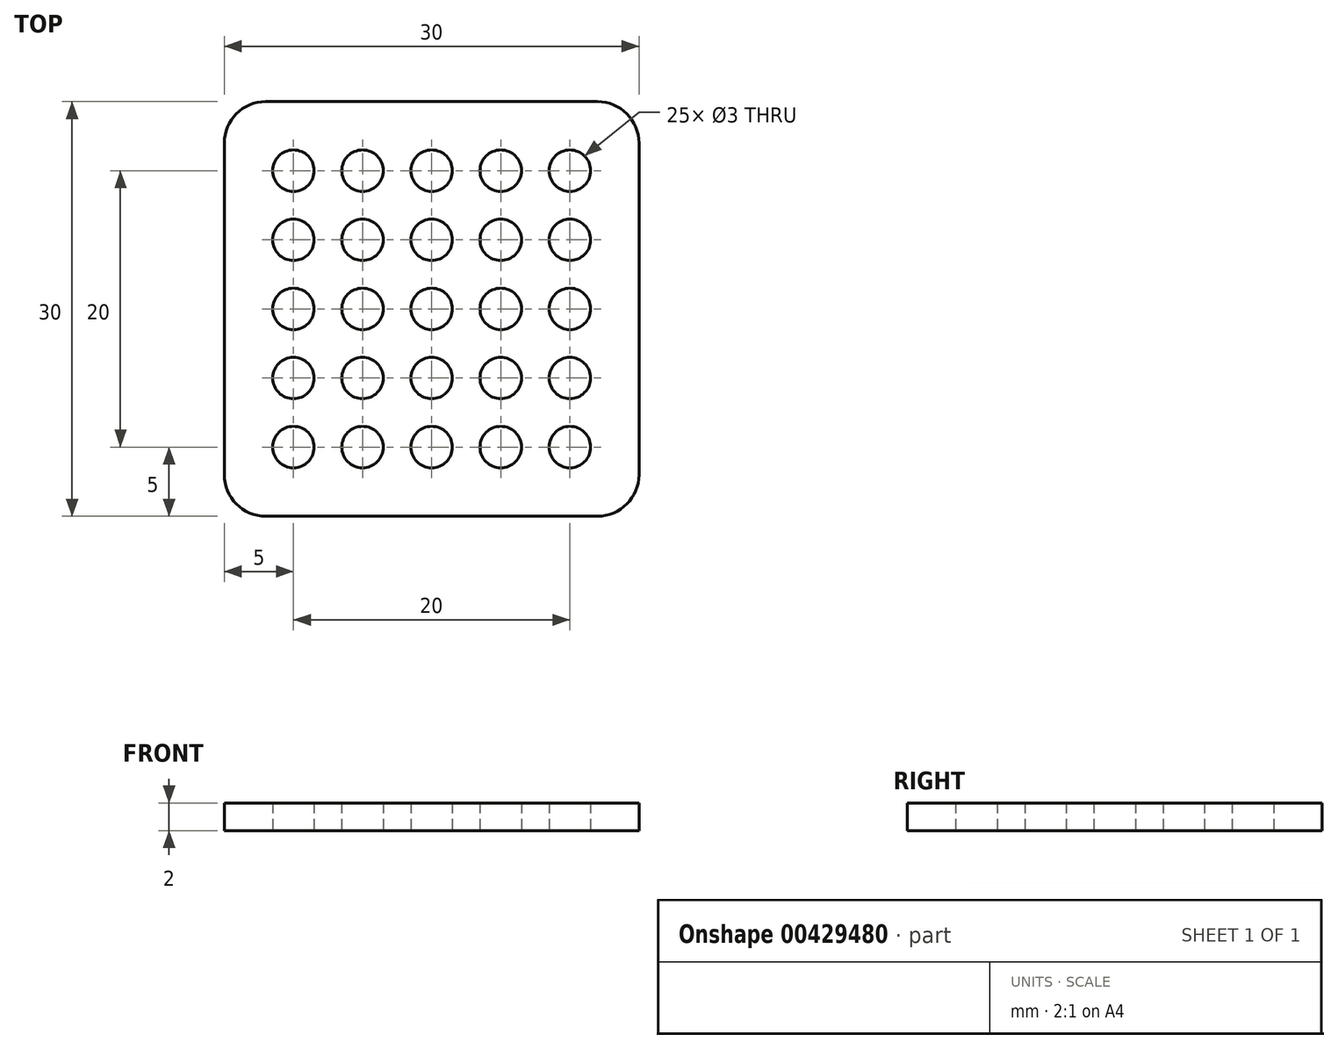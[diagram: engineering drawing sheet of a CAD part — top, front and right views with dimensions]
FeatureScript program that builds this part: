
annotation { "Feature Type Name" : "Feature", "Feature Type Description" : "" }
export const myFeature = defineFeature(function(context is Context, id is Id, definition is map)
    precondition{}
    {
        {
            var Q0;
            Q0=qCreatedBy(makeId("Top.planeOp"),FACE);
            var sketch = newSketch(context, id + "F0", { "sketchPlane" : qUnion([Q0])});
            skLineSegment(sketch, "E0.bottom", {"start": v(12, -15) * mm, "end": v(-12, -15) * mm});
            skLineSegment(sketch, "E0.top", {"start": v(12, 15) * mm, "end": v(-12, 15) * mm});
            skLineSegment(sketch, "E0.left", {"start": v(15, -12) * mm, "end": v(15, 12) * mm});
            skLineSegment(sketch, "E0.right", {"start": v(-15, -12) * mm, "end": v(-15, 12) * mm});
            skPoint(sketch, "E0.middle", {"position": v(0, 0) * mm});
            skPoint(sketch, "E1.visualSharp", {"position": v(-15, 15) * mm});
            skArc(sketch, "E1.filletArc", {"start": v(-12, 15) * mm, "mid": v(-14.12, 14.12) * mm, "end": v(-15, 12) * mm});
            skPoint(sketch, "E2.visualSharp", {"position": v(15, 15) * mm});
            skArc(sketch, "E2.filletArc", {"start": v(15, 12) * mm, "mid": v(14.12, 14.12) * mm, "end": v(12, 15) * mm});
            skPoint(sketch, "E3.visualSharp", {"position": v(15, -15) * mm});
            skArc(sketch, "E3.filletArc", {"start": v(12, -15) * mm, "mid": v(14.12, -14.12) * mm, "end": v(15, -12) * mm});
            skPoint(sketch, "E4.visualSharp", {"position": v(-15, -15) * mm});
            skArc(sketch, "E4.filletArc", {"start": v(-15, -12) * mm, "mid": v(-14.12, -14.12) * mm, "end": v(-12, -15) * mm});
            skCircle(sketch, "E5", {"center": v(-10, -10) * mm, "radius": 1.5 * mm});
            skCircle(sketch, "E6.0.1.0", {"center": v(-10, -5) * mm, "radius": 1.5 * mm});
            skCircle(sketch, "E6.0.2.0", {"center": v(-10, 0) * mm, "radius": 1.5 * mm});
            skCircle(sketch, "E6.0.3.0", {"center": v(-10, 5) * mm, "radius": 1.5 * mm});
            skCircle(sketch, "E6.0.4.0", {"center": v(-10, 10) * mm, "radius": 1.5 * mm});
            skCircle(sketch, "E6.1.0.0", {"center": v(-5, -10) * mm, "radius": 1.5 * mm});
            skCircle(sketch, "E6.1.1.0", {"center": v(-5, -5) * mm, "radius": 1.5 * mm});
            skCircle(sketch, "E6.1.2.0", {"center": v(-5, 0) * mm, "radius": 1.5 * mm});
            skCircle(sketch, "E6.1.3.0", {"center": v(-5, 5) * mm, "radius": 1.5 * mm});
            skCircle(sketch, "E6.1.4.0", {"center": v(-5, 10) * mm, "radius": 1.5 * mm});
            skCircle(sketch, "E6.2.0.0", {"center": v(0, -10) * mm, "radius": 1.5 * mm});
            skCircle(sketch, "E6.2.1.0", {"center": v(0, -5) * mm, "radius": 1.5 * mm});
            skCircle(sketch, "E6.2.2.0", {"center": v(0, 0) * mm, "radius": 1.5 * mm});
            skCircle(sketch, "E6.2.3.0", {"center": v(0, 5) * mm, "radius": 1.5 * mm});
            skCircle(sketch, "E6.2.4.0", {"center": v(0, 10) * mm, "radius": 1.5 * mm});
            skCircle(sketch, "E6.3.0.0", {"center": v(5, -10) * mm, "radius": 1.5 * mm});
            skCircle(sketch, "E6.3.1.0", {"center": v(5, -5) * mm, "radius": 1.5 * mm});
            skCircle(sketch, "E6.3.2.0", {"center": v(5, 0) * mm, "radius": 1.5 * mm});
            skCircle(sketch, "E6.3.3.0", {"center": v(5, 5) * mm, "radius": 1.5 * mm});
            skCircle(sketch, "E6.3.4.0", {"center": v(5, 10) * mm, "radius": 1.5 * mm});
            skCircle(sketch, "E6.4.0.0", {"center": v(10, -10) * mm, "radius": 1.5 * mm});
            skCircle(sketch, "E6.4.1.0", {"center": v(10, -5) * mm, "radius": 1.5 * mm});
            skCircle(sketch, "E6.4.2.0", {"center": v(10, 0) * mm, "radius": 1.5 * mm});
            skCircle(sketch, "E6.4.3.0", {"center": v(10, 5) * mm, "radius": 1.5 * mm});
            skCircle(sketch, "E6.4.4.0", {"center": v(10, 10) * mm, "radius": 1.5 * mm});
            skLineSegment(sketch, "E6.direction1", {"start": v(-10, -10) * mm, "end": v(-5, -10) * mm, "construction": true});
            skLineSegment(sketch, "E6.direction2", {"start": v(-10, -10) * mm, "end": v(-10, -5) * mm, "construction": true});
            skSolve(sketch);
        }
        {
            var Q0;
            Q0=makeQuery(id+"F0.imprint","IMPRINT",FACE,{"disambiguationData":[TD([[makeQuery(id+"F0.imprint","IMPRINT",EDGE,{"derivedFrom":sQuery(id+"F0.wireOp",EDGE,"E0.bottom")}),-1.0]])]});
            extrude(context, id + "F1", {"entities" : qUnion([Q0]), "depth" : 2 * mm});
        }
    });
